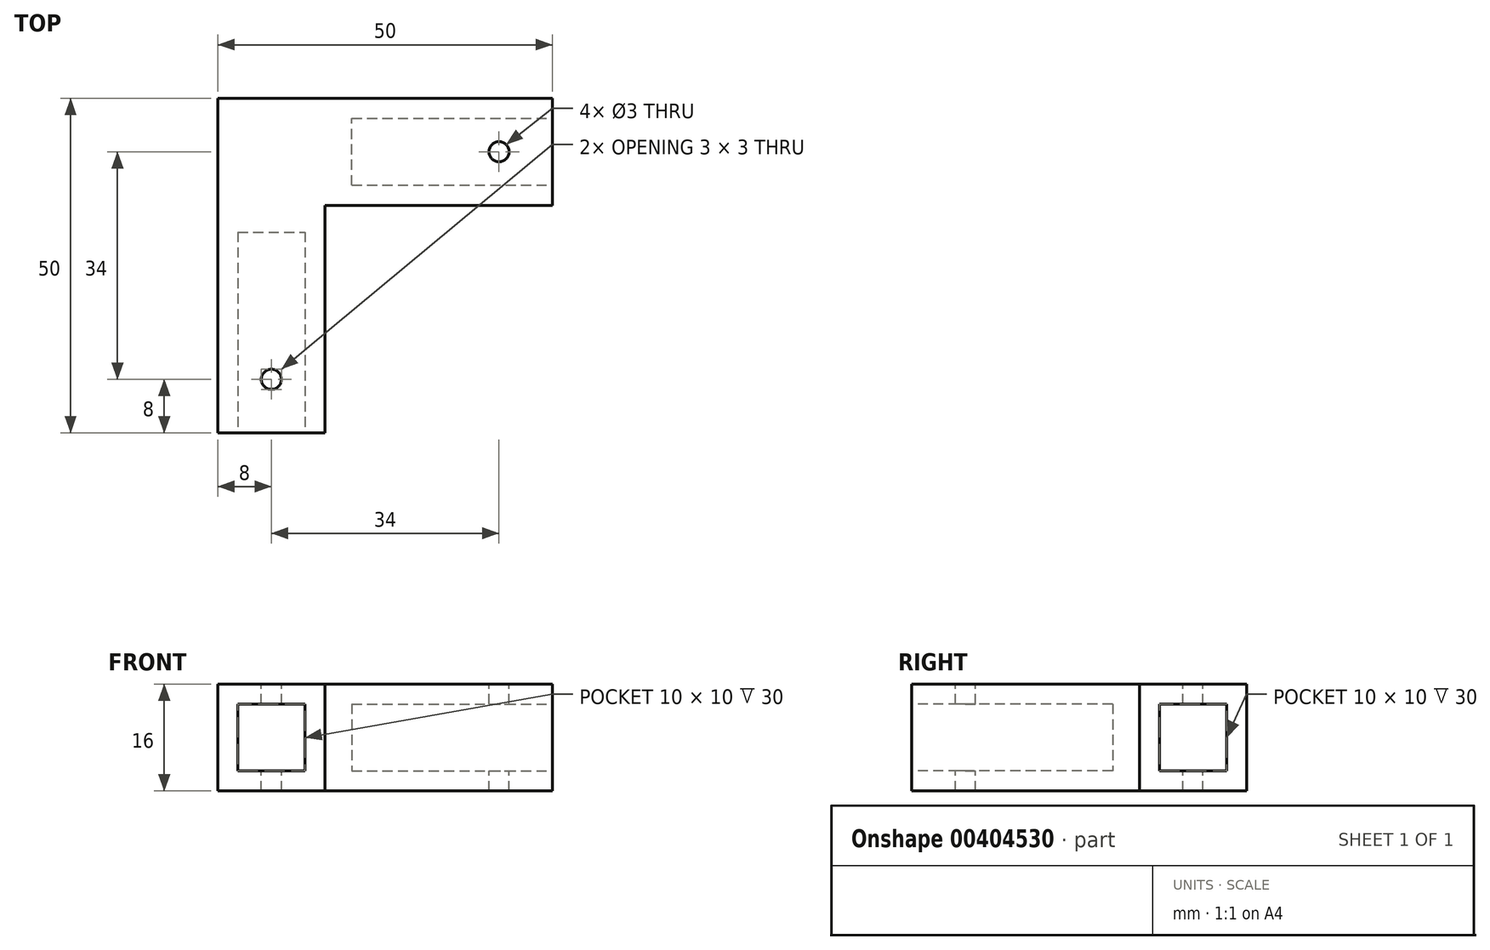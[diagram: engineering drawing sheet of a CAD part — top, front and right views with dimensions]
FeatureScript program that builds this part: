
annotation { "Feature Type Name" : "Feature", "Feature Type Description" : "" }
export const myFeature = defineFeature(function(context is Context, id is Id, definition is map)
    precondition{}
    {
        {
            var Q0;
            Q0=qCreatedBy(makeId("Top.planeOp"),FACE);
            var sketch = newSketch(context, id + "F0", { "sketchPlane" : qUnion([Q0])});
            skLineSegment(sketch, "E0.bottom", {"start": v(-25, 16) * mm, "end": v(25, 16) * mm});
            skLineSegment(sketch, "E0.top", {"start": v(-25, 0) * mm, "end": v(25, 0) * mm});
            skLineSegment(sketch, "E0.left", {"start": v(-25, 16) * mm, "end": v(-25, 0) * mm});
            skLineSegment(sketch, "E0.right", {"start": v(25, 16) * mm, "end": v(25, 0) * mm});
            skLineSegment(sketch, "E1.bottom", {"start": v(-25, 0) * mm, "end": v(-9, 0) * mm});
            skLineSegment(sketch, "E1.top", {"start": v(-25, -34) * mm, "end": v(-9, -34) * mm});
            skLineSegment(sketch, "E1.left", {"start": v(-25, 0) * mm, "end": v(-25, -34) * mm});
            skLineSegment(sketch, "E1.right", {"start": v(-9, 0) * mm, "end": v(-9, -34) * mm});
            skSolve(sketch);
        }
        {
            var Q0;
            Q0 = qSketchRegion(id + "F0", true);
            extrude(context, id + "F1", {"entities" : qUnion([Q0]), "depth" : 16 * mm});
        }
        {
            var Q0;
            Q0=makeQuery(id+"F1.opExtrude","SWEPT_FACE",FACE,{"disambiguationData":[OSD([sQuery(id+"F0.wireOp",EDGE,"E0.right")])]});
            var sketch = newSketch(context, id + "F2", { "sketchPlane" : qUnion([Q0])});
            skLineSegment(sketch, "E2.bottom", {"start": v(3, 13) * mm, "end": v(13, 13) * mm});
            skLineSegment(sketch, "E2.top", {"start": v(3, 3) * mm, "end": v(13, 3) * mm});
            skLineSegment(sketch, "E2.left", {"start": v(3, 13) * mm, "end": v(3, 3) * mm});
            skLineSegment(sketch, "E2.right", {"start": v(13, 13) * mm, "end": v(13, 3) * mm});
            skSolve(sketch);
        }
        {
            var Q0;
            Q0 = qSketchRegion(id + "F2", true);
            extrude(context, id + "F3", {"entities" : qUnion([Q0]), "operationType" : NewBodyOperationType.REMOVE, "oppositeDirection" : true, "depth" : 30 * mm});
        }
        {
            var Q0;
            Q0=makeQuery(id+"F1.opExtrude","SWEPT_FACE",FACE,{"disambiguationData":[OSD([sQuery(id+"F0.wireOp",EDGE,"E1.top")])]});
            var sketch = newSketch(context, id + "F4", { "sketchPlane" : qUnion([Q0])});
            skLineSegment(sketch, "E3.bottom", {"start": v(-22, 13) * mm, "end": v(-12, 13) * mm});
            skLineSegment(sketch, "E3.top", {"start": v(-22, 3) * mm, "end": v(-12, 3) * mm});
            skLineSegment(sketch, "E3.left", {"start": v(-22, 13) * mm, "end": v(-22, 3) * mm});
            skLineSegment(sketch, "E3.right", {"start": v(-12, 13) * mm, "end": v(-12, 3) * mm});
            skSolve(sketch);
        }
        {
            var Q0;
            Q0 = qSketchRegion(id + "F4", true);
            extrude(context, id + "F5", {"entities" : qUnion([Q0]), "operationType" : NewBodyOperationType.REMOVE, "oppositeDirection" : true, "depth" : 30 * mm});
        }
        {
            var Q0;
            Q0=makeQuery(id+"F1.opExtrude","CAP_FACE",FACE,{"disambiguationData":[OSD([sQuery(id+"F0.wireOp",EDGE,"E0.bottom"),sQuery(id+"F0.wireOp",EDGE,"E0.top"),sQuery(id+"F0.wireOp",EDGE,"E0.left"),sQuery(id+"F0.wireOp",EDGE,"E0.right"),sQuery(id+"F0.wireOp",EDGE,"E1.top"),sQuery(id+"F0.wireOp",EDGE,"E1.left"),sQuery(id+"F0.wireOp",EDGE,"E1.right")])],"isStart":false});
            var sketch = newSketch(context, id + "F6", { "sketchPlane" : qUnion([Q0])});
            skCircle(sketch, "E4", {"center": v(-17, -26) * mm, "radius": 1.5 * mm});
            skCircle(sketch, "E5", {"center": v(17, 8) * mm, "radius": 1.5 * mm});
            skSolve(sketch);
        }
        {
            var Q0;
            Q0 = qSketchRegion(id + "F6", true);
            extrude(context, id + "F7", {"entities" : qUnion([Q0]), "operationType" : NewBodyOperationType.REMOVE, "oppositeDirection" : true, "depth" : 16 * mm});
        }
    });
